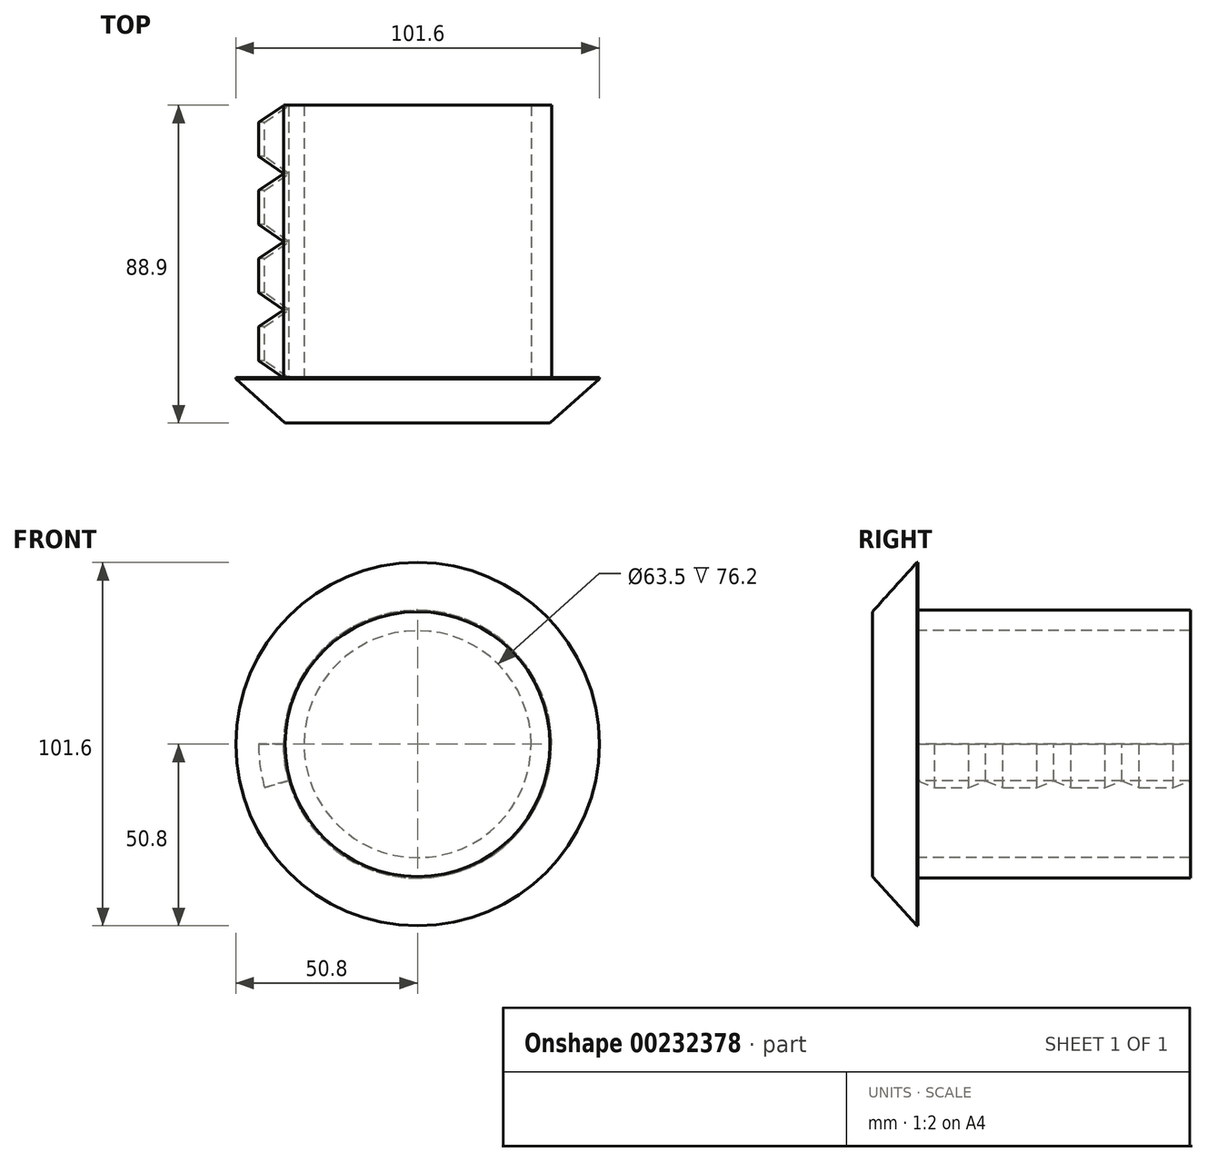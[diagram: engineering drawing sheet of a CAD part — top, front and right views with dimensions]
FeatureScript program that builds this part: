
annotation { "Feature Type Name" : "Feature", "Feature Type Description" : "" }
export const myFeature = defineFeature(function(context is Context, id is Id, definition is map)
    precondition{}
    {
        {
            var Q0;
            Q0=qCreatedBy(makeId("Front.planeOp"),FACE);
            var sketch = newSketch(context, id + "F0", { "sketchPlane" : qUnion([Q0])});
            skCircle(sketch, "E0", {"center": v(0, 0) * mm, "radius": 50.8 * mm});
            skSolve(sketch);
        }
        {
            var Q0;
            Q0=makeQuery(id+"F0.imprint","IMPRINT",FACE,{"disambiguationData":[TD([[makeQuery(id+"F0.imprint","IMPRINT",EDGE,{"derivedFrom":sQuery(id+"F0.wireOp",EDGE,"E0")}),1.0]])]});
            extrude(context, id + "F1", {"entities" : qUnion([Q0]), "depth" : 12.7 * mm});
        }
        {
            var Q0;
            Q0=qCreatedBy(makeId("Right.planeOp"),FACE);
            var sketch = newSketch(context, id + "F2", { "sketchPlane" : qUnion([Q0])});
            skLineSegment(sketch, "E1", {"start": v(0, -51.15) * mm, "end": v(-12.9, -36.82) * mm});
            skLineSegment(sketch, "E2", {"start": v(-12.9, -36.82) * mm, "end": v(-12.9, -50.86) * mm});
            skLineSegment(sketch, "E3", {"start": v(-12.9, -50.86) * mm, "end": v(0, -51.15) * mm});
            skSolve(sketch);
        }
        {
            var Q0;
            Q0 = qSketchRegion(id + "F2", true);
            var Q1;
            Q1=makeQuery(id+"F1.opExtrude","SWEPT_FACE",FACE,{"disambiguationData":[OSD([sQuery(id+"F0.wireOp",EDGE,"E0")])]});
            revolve(context, id + "F3", {"operationType" : NewBodyOperationType.REMOVE, "entities" : qUnion([Q0]), "axis" : qUnion([Q1]), "revolveType" : RevolveType.ONE_DIRECTION, "oppositeDirection" : true, "angle" : 360 * degree});
        }
        {
            var Q0;
            Q0 = qSketchRegion(id + "F2", true);
            extrude(context, id + "F4", {"entities" : qUnion([Q0]), "operationType" : NewBodyOperationType.REMOVE, "oppositeDirection" : true, "depth" : 25.4 * mm});
        }
        {
            var Q0;
            Q0=qCreatedBy(makeId("Front.planeOp"),FACE);
            var sketch = newSketch(context, id + "F5", { "sketchPlane" : qUnion([Q0])});
            skCircle(sketch, "E4", {"center": v(0, 0) * mm, "radius": 37.47 * mm});
            skCircle(sketch, "E5", {"center": v(0, 0) * mm, "radius": 31.75 * mm});
            skSolve(sketch);
        }
        {
            var Q0;
            Q0=makeQuery(id+"F5.imprint","IMPRINT",FACE,{"disambiguationData":[TD([[makeQuery(id+"F5.imprint","IMPRINT",EDGE,{"derivedFrom":sQuery(id+"F5.wireOp",EDGE,"E4")}),1.0]])]});
            extrude(context, id + "F6", {"entities" : qUnion([Q0]), "operationType" : NewBodyOperationType.ADD, "oppositeDirection" : true, "depth" : 76.2 * mm});
        }
        {
            var Q0;
            Q0=qCreatedBy(makeId("Top.planeOp"),FACE);
            var sketch = newSketch(context, id + "F7", { "sketchPlane" : qUnion([Q0])});
            skLineSegment(sketch, "E6", {"start": v(-37.46, 76.12) * mm, "end": v(-37.46, 57.07) * mm});
            skLineSegment(sketch, "E7", {"start": v(-37.46, 57.07) * mm, "end": v(-44.45, 61.84) * mm});
            skLineSegment(sketch, "E8", {"start": v(-44.45, 61.84) * mm, "end": v(-44.45, 71.36) * mm});
            skLineSegment(sketch, "E9", {"start": v(-44.45, 71.36) * mm, "end": v(-37.47, 76.12) * mm});
            skLineSegment(sketch, "E10", {"start": v(-37.46, 57.07) * mm, "end": v(-37.46, 38.02) * mm});
            skLineSegment(sketch, "E11", {"start": v(-37.47, 38.02) * mm, "end": v(-44.45, 42.79) * mm});
            skLineSegment(sketch, "E12", {"start": v(-44.45, 42.79) * mm, "end": v(-44.45, 52.31) * mm});
            skLineSegment(sketch, "E13", {"start": v(-44.45, 52.31) * mm, "end": v(-37.47, 57.07) * mm});
            skLineSegment(sketch, "E14", {"start": v(-37.47, 38.02) * mm, "end": v(-37.47, 18.97) * mm});
            skLineSegment(sketch, "E15", {"start": v(-37.46, 18.97) * mm, "end": v(-44.45, 23.74) * mm});
            skLineSegment(sketch, "E16", {"start": v(-44.45, 23.74) * mm, "end": v(-44.45, 33.26) * mm});
            skLineSegment(sketch, "E17", {"start": v(-44.45, 33.26) * mm, "end": v(-37.47, 38.02) * mm});
            skLineSegment(sketch, "E18", {"start": v(-37.47, 18.97) * mm, "end": v(-37.46, -0.08) * mm});
            skLineSegment(sketch, "E19", {"start": v(-37.46, -0.08) * mm, "end": v(-44.45, 4.69) * mm});
            skLineSegment(sketch, "E20", {"start": v(-44.45, 4.69) * mm, "end": v(-44.45, 14.21) * mm});
            skLineSegment(sketch, "E21", {"start": v(-44.45, 14.21) * mm, "end": v(-37.47, 18.97) * mm});
            skSolve(sketch);
        }
        {
            var Q0;
            Q0 = qSketchRegion(id + "F7", true);
            var Q1;
            Q1=makeQuery(id+"F6.opExtrude","CAP_EDGE",EDGE,{"disambiguationData":[OSD([sQuery(id+"F5.wireOp",EDGE,"E4")])],"isStart":false});
            revolve(context, id + "F8", {"operationType" : NewBodyOperationType.ADD, "entities" : qUnion([Q0]), "axis" : qUnion([Q1]), "revolveType" : RevolveType.ONE_DIRECTION, "angle" : 15.83 * degree});
        }
    });
